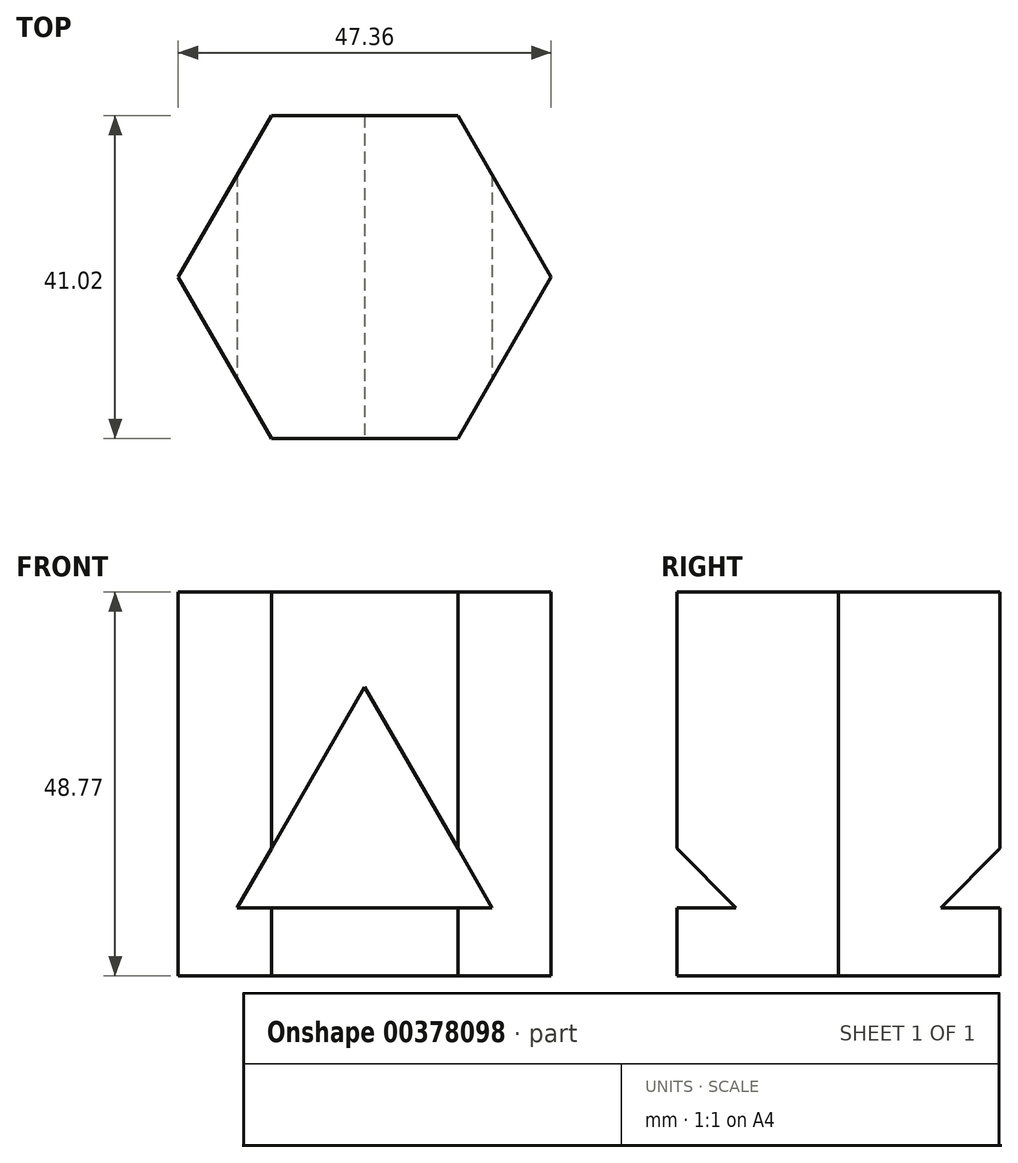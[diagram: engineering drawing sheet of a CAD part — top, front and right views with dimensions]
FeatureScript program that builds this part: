
annotation { "Feature Type Name" : "Feature", "Feature Type Description" : "" }
export const myFeature = defineFeature(function(context is Context, id is Id, definition is map)
    precondition{}
    {
        {
            var Q0;
            Q0=qCreatedBy(makeId("Top.planeOp"),FACE);
            var sketch = newSketch(context, id + "F0", { "sketchPlane" : qUnion([Q0])});
            skCircle(sketch, "E0.cCircle", {"center": v(0, 0) * mm, "radius": 20.5 * mm, "construction": true});
            skLineSegment(sketch, "E0.0", {"start": v(-11.84, 20.5) * mm, "end": v(11.84, 20.5) * mm});
            skLineSegment(sketch, "E0.1", {"start": v(11.84, 20.5) * mm, "end": v(23.68, 0) * mm});
            skLineSegment(sketch, "E0.2", {"start": v(23.68, 0) * mm, "end": v(11.84, -20.5) * mm});
            skLineSegment(sketch, "E0.3", {"start": v(11.84, -20.5) * mm, "end": v(-11.84, -20.5) * mm});
            skLineSegment(sketch, "E0.4", {"start": v(-11.84, -20.5) * mm, "end": v(-23.68, 0) * mm});
            skLineSegment(sketch, "E0.5", {"start": v(-23.68, 0) * mm, "end": v(-11.84, 20.5) * mm});
            skPoint(sketch, "E0.0.midPoint", {"position": v(0, 20.5) * mm});
            skSolve(sketch);
        }
        {
            var Q0;
            Q0 = qSketchRegion(id + "F0", true);
            extrude(context, id + "F1", {"entities" : qUnion([Q0]), "depth" : 48.77 * mm});
        }
        {
            var Q0;
            Q0=qCreatedBy(makeId("Front.planeOp"),FACE);
            var sketch = newSketch(context, id + "F2", { "sketchPlane" : qUnion([Q0])});
            skCircle(sketch, "E1.cCircle", {"center": v(0, 18) * mm, "radius": 9.34 * mm, "construction": true});
            skLineSegment(sketch, "E1.0", {"start": v(0, 36.68) * mm, "end": v(16.18, 8.67) * mm});
            skLineSegment(sketch, "E1.1", {"start": v(16.18, 8.67) * mm, "end": v(-16.18, 8.67) * mm});
            skLineSegment(sketch, "E1.2", {"start": v(-16.18, 8.67) * mm, "end": v(0, 36.68) * mm});
            skPoint(sketch, "E1.0.midPoint", {"position": v(8.09, 22.67) * mm});
            skSolve(sketch);
        }
        {
            var Q0;
            Q0 = qSketchRegion(id + "F2", true);
            extrude(context, id + "F3", {"entities" : qUnion([Q0]), "operationType" : NewBodyOperationType.REMOVE, "endBound" : BoundingType.SYMMETRIC, "oppositeDirection" : true, "depth" : 83.82 * mm});
        }
    });
